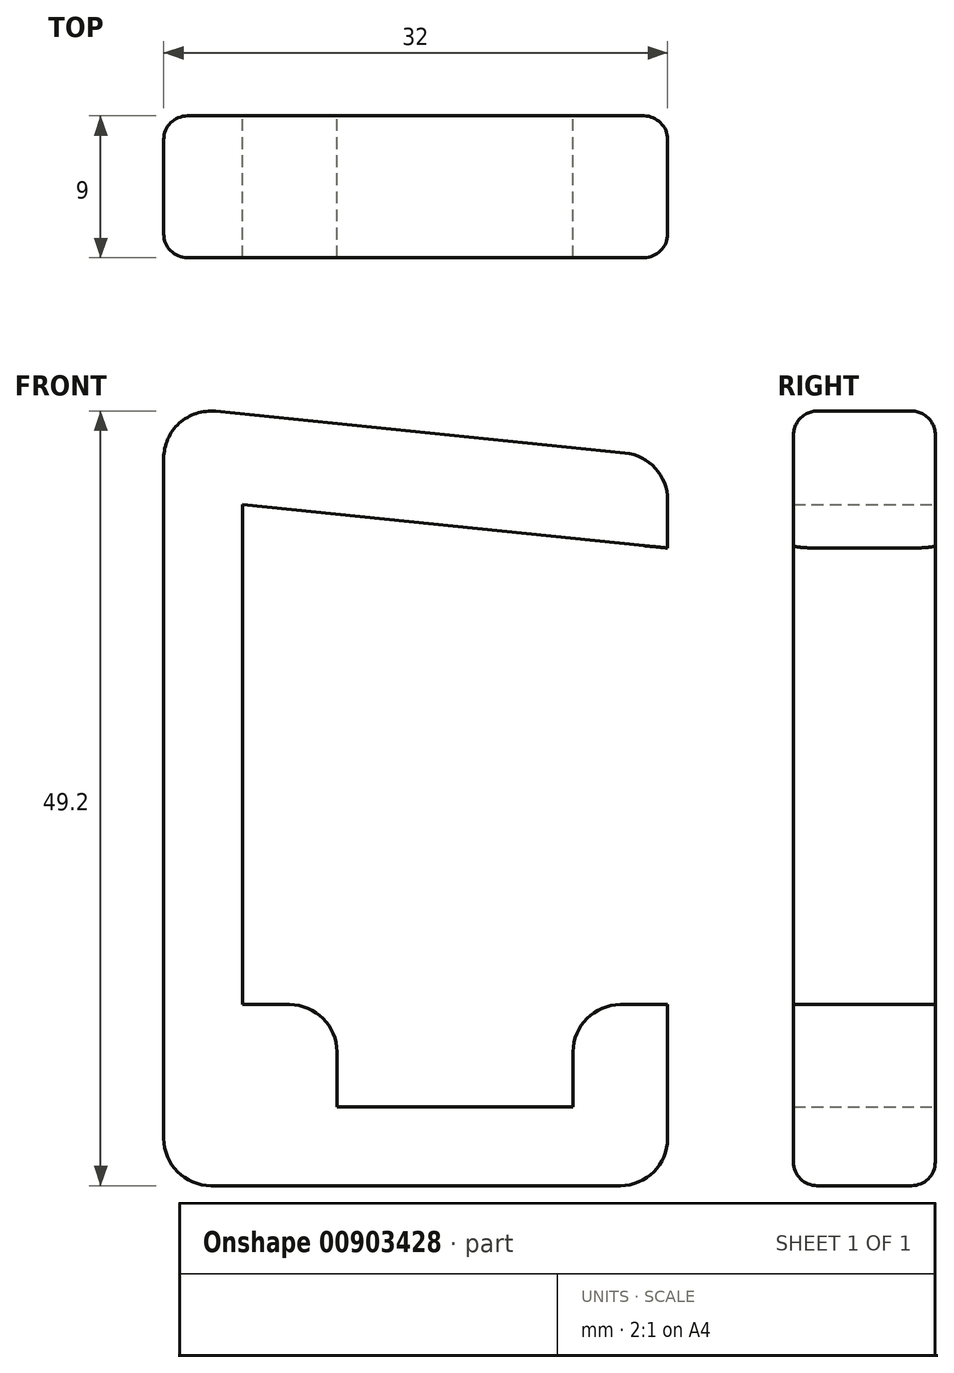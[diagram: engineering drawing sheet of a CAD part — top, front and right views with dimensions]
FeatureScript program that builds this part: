
annotation { "Feature Type Name" : "Feature", "Feature Type Description" : "" }
export const myFeature = defineFeature(function(context is Context, id is Id, definition is map)
    precondition{}
    {
        {
            var Q0;
            Q0=qCreatedBy(makeId("Front.planeOp"),FACE);
            var sketch = newSketch(context, id + "F0", { "sketchPlane" : qUnion([Q0])});
            skLineSegment(sketch, "E0", {"start": v(44.05, 0) * mm, "end": v(-58.7, 0) * mm, "construction": true});
            skLineSegment(sketch, "E1", {"start": v(-40.04, 35.36) * mm, "end": v(-40.04, -18.02) * mm, "construction": true});
            skLineSegment(sketch, "E2", {"start": v(-13.04, 29) * mm, "end": v(-40.04, 31.75) * mm});
            skLineSegment(sketch, "E3", {"start": v(-40.04, 31.75) * mm, "end": v(-40.04, 0) * mm});
            skLineSegment(sketch, "E4", {"start": v(-40.04, 0) * mm, "end": v(-37.04, 0) * mm});
            skLineSegment(sketch, "E5", {"start": v(-34.04, -3) * mm, "end": v(-34.04, -6.5) * mm});
            skLineSegment(sketch, "E6", {"start": v(-34.04, -6.5) * mm, "end": v(-19.04, -6.5) * mm});
            skLineSegment(sketch, "E7", {"start": v(-19.04, -6.5) * mm, "end": v(-19.04, -3) * mm});
            skLineSegment(sketch, "E8", {"start": v(-16.04, 0) * mm, "end": v(-13.04, 0) * mm});
            skLineSegment(sketch, "E9", {"start": v(-13.04, 0) * mm, "end": v(-13.04, -8.5) * mm});
            skLineSegment(sketch, "E10", {"start": v(-16.04, -11.5) * mm, "end": v(-42.04, -11.5) * mm});
            skLineSegment(sketch, "E11", {"start": v(-45.04, -8.5) * mm, "end": v(-45.04, 34.7) * mm});
            skLineSegment(sketch, "E12", {"start": v(-41.74, 37.68) * mm, "end": v(-15.74, 35.04) * mm});
            skLineSegment(sketch, "E13", {"start": v(-13.04, 32.05) * mm, "end": v(-13.04, 29) * mm});
            skPoint(sketch, "E14.visualSharp", {"position": v(-45.04, 38.02) * mm});
            skArc(sketch, "E14.filletArc", {"start": v(-41.74, 37.68) * mm, "mid": v(-44.05, 36.93) * mm, "end": v(-45.04, 34.7) * mm});
            skPoint(sketch, "E15.visualSharp", {"position": v(-45.04, -11.5) * mm});
            skArc(sketch, "E15.filletArc", {"start": v(-45.04, -8.5) * mm, "mid": v(-44.16, -10.62) * mm, "end": v(-42.04, -11.5) * mm});
            skArc(sketch, "E16.filletArc", {"start": v(-13.04, 32.05) * mm, "mid": v(-13.81, 34.06) * mm, "end": v(-15.74, 35.04) * mm});
            skPoint(sketch, "E17.visualSharp", {"position": v(-13.04, -11.5) * mm});
            skArc(sketch, "E17.filletArc", {"start": v(-16.04, -11.5) * mm, "mid": v(-13.92, -10.62) * mm, "end": v(-13.04, -8.5) * mm});
            skPoint(sketch, "E18.visualSharp", {"position": v(-34.04, 0) * mm});
            skArc(sketch, "E18.filletArc", {"start": v(-34.04, -3) * mm, "mid": v(-34.92, -0.88) * mm, "end": v(-37.04, 0) * mm});
            skPoint(sketch, "E19.visualSharp", {"position": v(-19.04, 0) * mm});
            skArc(sketch, "E19.filletArc", {"start": v(-16.04, 0) * mm, "mid": v(-18.16, -0.88) * mm, "end": v(-19.04, -3) * mm});
            skLineSegment(sketch, "E20", {"start": v(-47, 31.75) * mm, "end": v(-11.52, 31.75) * mm, "construction": true});
            skSolve(sketch);
        }
        {
            var Q0;
            Q0 = qSketchRegion(id + "F0", true);
            extrude(context, id + "F1", {"entities" : qUnion([Q0]), "depth" : 9 * mm, "offsetDistance" : 25 * mm});
        }
        {
            var Q0;
            Q0=makeQuery(id+"F1.opExtrude","CAP_EDGE",EDGE,{"disambiguationData":[OSD([sQuery(id+"F0.wireOp",EDGE,"E10")])],"isStart":false});
            var Q1;
            Q1=makeQuery(id+"F1.opExtrude","CAP_EDGE",EDGE,{"disambiguationData":[OSD([sQuery(id+"F0.wireOp",EDGE,"E11")])],"isStart":true});
            fillet(context, id + "F2", {"entities" : qUnion([Q0, Q1]), "radius" : 1.5 * mm, "tangentPropagation" : true, "allowEdgeOverflow" : false});
        }
    });
